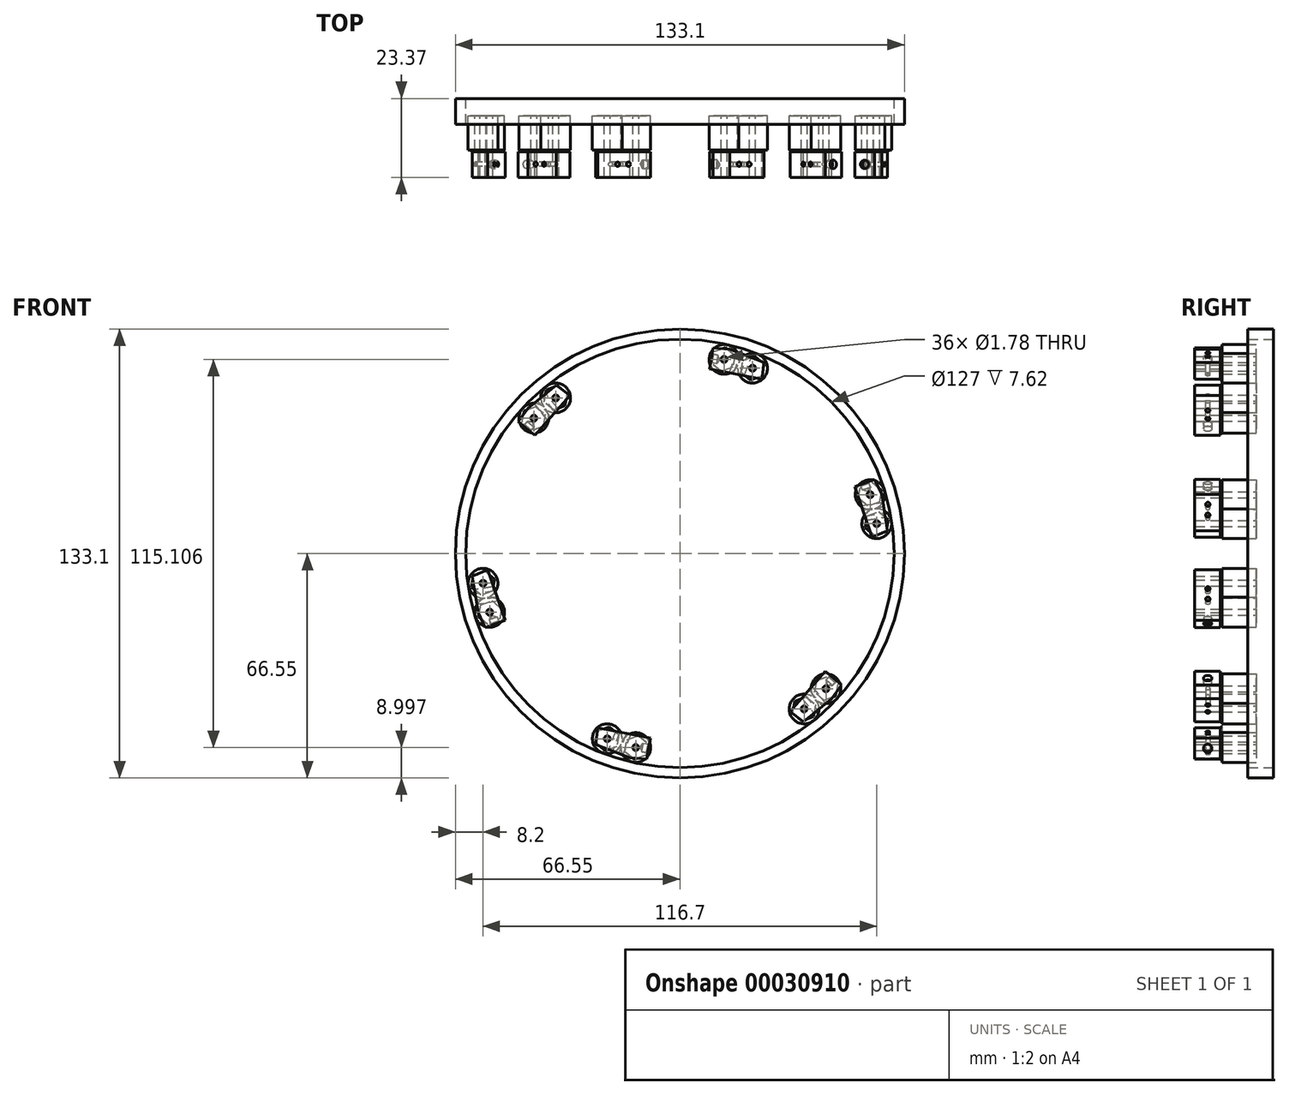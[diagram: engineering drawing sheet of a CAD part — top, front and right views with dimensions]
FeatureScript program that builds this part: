
annotation { "Feature Type Name" : "Feature", "Feature Type Description" : "" }
export const myFeature = defineFeature(function(context is Context, id is Id, definition is map)
    precondition{}
    {
        {
            var Q0;
            Q0=qCreatedBy(makeId("Front.planeOp"),FACE);
            var sketch = newSketch(context, id + "F0", { "sketchPlane" : qUnion([Q0])});
            skCircle(sketch, "E0", {"center": v(0, 0) * mm, "radius": 66.55 * mm});
            skSolve(sketch);
        }
        {
            var Q0;
            Q0=makeQuery(id+"F0.imprint","IMPRINT",FACE,{"disambiguationData":[TD([[makeQuery(id+"F0.imprint","IMPRINT",EDGE,{"derivedFrom":sQuery(id+"F0.wireOp",EDGE,"E0")}),1.0]])]});
            extrude(context, id + "F1", {"entities" : qUnion([Q0]), "depth" : 7.62 * mm});
        }
        {
            var Q0;
            Q0=sQuery(id+"F0.wireOp",VERTEX,"E0.center");
            var Q1;
            Q1=makeQuery(id+"F1.opExtrude","SWEPT_BODY",BODY,{"disambiguationData":[OSD([sQuery(id+"F0.wireOp",EDGE,"E0")])]});
            hole(context, id + "F2", {"style" : HoleStyle.SIMPLE, "holeDiameter" : 127 * mm, "endStyle" : HoleEndStyle.THROUGH, "oppositeDirection" : true, "locations" : qUnion([Q0]), "scope" : qUnion([Q1])});
        }
        {
            var Q0;
            Q0=qCreatedBy(makeId("Front.planeOp"),FACE);
            var sketch = newSketch(context, id + "F3", { "sketchPlane" : qUnion([Q0])});
            skCircle(sketch, "E1", {"center": v(13.1, 57.55) * mm, "radius": 4.4 * mm});
            skPoint(sketch, "E1.first.point", {"position": v(14.07, 61.85) * mm});
            skPoint(sketch, "E1.second.point", {"position": v(11.49, 53.45) * mm});
            skPoint(sketch, "E1.third.point", {"position": v(11.97, 53.29) * mm});
            skCircle(sketch, "E2", {"center": v(21.53, 54.95) * mm, "radius": 4.4 * mm});
            skSolve(sketch);
        }
        {
            var Q0;
            Q0=makeQuery(id+"F3.imprint","IMPRINT",FACE,{"disambiguationData":[TD([[makeQuery(id+"F3.imprint","IMPRINT",EDGE,{"derivedFrom":sQuery(id+"F3.wireOp",EDGE,"E2")}),1.0]])]});
            var Q1;
            Q1=makeQuery(id+"F3.imprint","IMPRINT",FACE,{"disambiguationData":[TD([[makeQuery(id+"F3.imprint","IMPRINT",EDGE,{"derivedFrom":sQuery(id+"F3.wireOp",EDGE,"E1")}),1.0]])]});
            extrude(context, id + "F4", {"entities" : qUnion([Q0, Q1]), "depth" : 15.24 * mm, "hasSecondDirection" : true, "secondDirectionOppositeDirection" : false, "secondDirectionDepth" : 5.08 * mm});
        }
        {
            var Q0;
            Q0=makeQuery(id+"F4.opExtrude","CAP_FACE",FACE,{"disambiguationData":[OSD([sQuery(id+"F3.wireOp",EDGE,"E2")])],"isStart":false});
            var sketch = newSketch(context, id + "F5", { "sketchPlane" : qUnion([Q0])});
            skCircle(sketch, "E3.cCircle", {"center": v(21.53, 54.95) * mm, "radius": 3.13 * mm, "construction": true});
            skLineSegment(sketch, "E3.0", {"start": v(24.3, 52.62) * mm, "end": v(20.9, 51.39) * mm});
            skLineSegment(sketch, "E3.1", {"start": v(20.9, 51.39) * mm, "end": v(18.14, 53.71) * mm});
            skLineSegment(sketch, "E3.2", {"start": v(18.14, 53.71) * mm, "end": v(18.77, 57.27) * mm});
            skLineSegment(sketch, "E3.3", {"start": v(18.77, 57.27) * mm, "end": v(22.16, 58.5) * mm});
            skLineSegment(sketch, "E3.4", {"start": v(22.16, 58.5) * mm, "end": v(24.93, 56.18) * mm});
            skLineSegment(sketch, "E3.5", {"start": v(24.93, 56.18) * mm, "end": v(24.3, 52.62) * mm});
            skPoint(sketch, "E3.0.midPoint", {"position": v(22.6, 52) * mm});
            skLineSegment(sketch, "E4.1", {"start": v(12.3, 54) * mm, "end": v(9.52, 56.32) * mm});
            skLineSegment(sketch, "E4.2", {"start": v(9.52, 56.32) * mm, "end": v(10.16, 59.88) * mm});
            skLineSegment(sketch, "E4.3", {"start": v(10.16, 59.88) * mm, "end": v(13.55, 61.11) * mm});
            skLineSegment(sketch, "E4.4", {"start": v(13.55, 61.11) * mm, "end": v(16.32, 58.79) * mm});
            skLineSegment(sketch, "E4.5", {"start": v(16.32, 58.79) * mm, "end": v(15.69, 55.23) * mm});
            skLineSegment(sketch, "E4.0", {"start": v(15.69, 55.23) * mm, "end": v(12.3, 54) * mm});
            skCircle(sketch, "E4.cCircle", {"center": v(12.92, 57.55) * mm, "radius": 3.13 * mm, "construction": true});
            skSolve(sketch);
        }
        {
            var Q0;
            Q0=makeQuery(id+"F5.imprint","IMPRINT",FACE,{"disambiguationData":[TD([[makeQuery(id+"F5.imprint","IMPRINT",EDGE,{"derivedFrom":sQuery(id+"F5.wireOp",EDGE,"E3.0")}),-1.0]])]});
            var Q1;
            Q1=makeQuery(id+"F5.imprint","IMPRINT",FACE,{"disambiguationData":[TD([[makeQuery(id+"F5.imprint","IMPRINT",EDGE,{"derivedFrom":sQuery(id+"F5.wireOp",EDGE,"E4.1")}),-1.0]])]});
            extrude(context, id + "F6", {"entities" : qUnion([Q0, Q1]), "depth" : 0.5 * mm});
        }
        {
            var Q0;
            Q0=makeQuery(id+"F6.opExtrude","CAP_FACE",FACE,{"disambiguationData":[OSD([sQuery(id+"F5.wireOp",EDGE,"E3.0"),sQuery(id+"F5.wireOp",EDGE,"E3.1"),sQuery(id+"F5.wireOp",EDGE,"E3.2"),sQuery(id+"F5.wireOp",EDGE,"E3.3"),sQuery(id+"F5.wireOp",EDGE,"E3.4"),sQuery(id+"F5.wireOp",EDGE,"E3.5")])],"isStart":false});
            var sketch = newSketch(context, id + "F7", { "sketchPlane" : qUnion([Q0])});
            skLineSegment(sketch, "E5", {"start": v(24.3, 51.72) * mm, "end": v(24.93, 56.67) * mm});
            skLineSegment(sketch, "E6", {"start": v(24.93, 56.67) * mm, "end": v(14.76, 60.55) * mm});
            skLineSegment(sketch, "E7", {"start": v(14.76, 60.55) * mm, "end": v(9.87, 61) * mm});
            skLineSegment(sketch, "E8", {"start": v(9.87, 61) * mm, "end": v(8.76, 54.78) * mm});
            skLineSegment(sketch, "E9", {"start": v(8.76, 54.78) * mm, "end": v(24.3, 51.72) * mm});
            skSolve(sketch);
        }
        {
            var Q0;
            {var subQ8=sQuery(id+"F7.wireOp",EDGE,"E7");Q0=makeQuery(id+"F7.imprint","IMPRINT",FACE,{"disambiguationData":[TD([[makeQuery(id+"F7.imprint","IMPRINT",EDGE,{"derivedFrom":subQ8}),1.0]])]});}
            var Q1;
            {var subQ11=makeQuery(id+"F6.opExtrude","CAP_EDGE",EDGE,{"disambiguationData":[OSD([sQuery(id+"F5.wireOp",EDGE,"E3.2")])],"isStart":false});Q1=makeQuery(id+"F7.imprint","IMPRINT",FACE,{"disambiguationData":[TD([[makeQuery(id+"F7.imprint","IMPRINT",EDGE,{"derivedFrom":subQ11}),-1.0]])]});}
            var Q2;
            {var subQ1=sQuery(id+"F7.wireOp",EDGE,"E5");var subQ5=sQuery(id+"F7.wireOp",EDGE,"E9");var subQ7=makeQuery(id+"F7.imprint","INTERSECT",VERTEX,{"derivedFrom":[subQ1,subQ5]});Q2=makeQuery(id+"F7.imprint","IMPRINT",FACE,{"disambiguationData":[TD([[makeQuery(id+"F7.imprint","IMPRINT",EDGE,{"disambiguationData":[TD([[subQ7,-1.0]])],"derivedFrom":subQ1}),1.0]])]});}
            var Q3;
            {var subQ1=sQuery(id+"F7.wireOp",EDGE,"E6");var subQ3=sQuery(id+"F7.wireOp",EDGE,"E5");var subQ5=makeQuery(id+"F7.imprint","INTERSECT",VERTEX,{"derivedFrom":[subQ3,subQ1]});Q3=makeQuery(id+"F7.imprint","IMPRINT",FACE,{"disambiguationData":[TD([[makeQuery(id+"F7.imprint","IMPRINT",EDGE,{"disambiguationData":[TD([[subQ5,1.0]])],"derivedFrom":subQ3}),1.0]])]});}
            extrude(context, id + "F8", {"entities" : qUnion([Q0, Q1, Q2, Q3]), "depth" : 7.62 * mm});
        }
        {
            var Q0;
            Q0=sQuery(id+"F3.wireOp",VERTEX,"E2.center");
            var Q1;
            Q1=makeQuery(id+"F4.opExtrude","SWEPT_BODY",BODY,{"disambiguationData":[OSD([sQuery(id+"F3.wireOp",EDGE,"E2")])]});
            var Q2;
            Q2=makeQuery(id+"F6.opExtrude","SWEPT_BODY",BODY,{"disambiguationData":[OSD([sQuery(id+"F5.wireOp",EDGE,"E3.0"),sQuery(id+"F5.wireOp",EDGE,"E3.1"),sQuery(id+"F5.wireOp",EDGE,"E3.2"),sQuery(id+"F5.wireOp",EDGE,"E3.3"),sQuery(id+"F5.wireOp",EDGE,"E3.4"),sQuery(id+"F5.wireOp",EDGE,"E3.5")])]});
            var Q3;
            Q3=makeQuery(id+"F8.opExtrude","SWEPT_BODY",BODY,{"disambiguationData":[OSD([sQuery(id+"F7.wireOp",EDGE,"E5"),sQuery(id+"F7.wireOp",EDGE,"E6"),sQuery(id+"F7.wireOp",EDGE,"E7"),sQuery(id+"F7.wireOp",EDGE,"E8"),sQuery(id+"F7.wireOp",EDGE,"E9")])]});
            hole(context, id + "F9", {"style" : HoleStyle.SIMPLE, "holeDiameter" : 1.78 * mm, "endStyle" : HoleEndStyle.THROUGH, "oppositeDirection" : true, "locations" : qUnion([Q0]), "scope" : qUnion([Q1, Q2, Q3])});
        }
        {
            var Q0;
            Q0=sQuery(id+"F3.wireOp",VERTEX,"E1.center");
            var Q1;
            Q1=makeQuery(id+"F4.opExtrude","SWEPT_BODY",BODY,{"disambiguationData":[OSD([sQuery(id+"F3.wireOp",EDGE,"E1")])]});
            var Q2;
            Q2=makeQuery(id+"F6.opExtrude","SWEPT_BODY",BODY,{"disambiguationData":[OSD([sQuery(id+"F5.wireOp",EDGE,"E4.1"),sQuery(id+"F5.wireOp",EDGE,"E4.2"),sQuery(id+"F5.wireOp",EDGE,"E4.3"),sQuery(id+"F5.wireOp",EDGE,"E4.4"),sQuery(id+"F5.wireOp",EDGE,"E4.5"),sQuery(id+"F5.wireOp",EDGE,"E4.0")])]});
            var Q3;
            Q3=makeQuery(id+"F8.opExtrude","SWEPT_BODY",BODY,{"disambiguationData":[OSD([sQuery(id+"F7.wireOp",EDGE,"E5"),sQuery(id+"F7.wireOp",EDGE,"E6"),sQuery(id+"F7.wireOp",EDGE,"E7"),sQuery(id+"F7.wireOp",EDGE,"E8"),sQuery(id+"F7.wireOp",EDGE,"E9")])]});
            hole(context, id + "F10", {"style" : HoleStyle.SIMPLE, "holeDiameter" : 1.78 * mm, "endStyle" : HoleEndStyle.THROUGH, "oppositeDirection" : true, "locations" : qUnion([Q0]), "scope" : qUnion([Q1, Q2, Q3])});
        }
        {
            var Q0;
            Q0=makeQuery(id+"F8.opExtrude","SWEPT_FACE",FACE,{"disambiguationData":[OSD([sQuery(id+"F7.wireOp",EDGE,"E6")])]});
            var sketch = newSketch(context, id + "F11", { "sketchPlane" : qUnion([Q0])});
            skCircle(sketch, "E10", {"center": v(-4.86, -19.5) * mm, "radius": 0.82 * mm});
            skCircle(sketch, "E11", {"center": v(-1.64, -19.51) * mm, "radius": 0.82 * mm});
            skSolve(sketch);
        }
        {
            var Q0;
            Q0=sQuery(id+"F11.wireOp",VERTEX,"E10.center");
            var Q1;
            Q1=sQuery(id+"F11.wireOp",VERTEX,"E11.center");
            var Q2;
            Q2=makeQuery(id+"F8.opExtrude","SWEPT_BODY",BODY,{"disambiguationData":[OSD([sQuery(id+"F7.wireOp",EDGE,"E5"),sQuery(id+"F7.wireOp",EDGE,"E6"),sQuery(id+"F7.wireOp",EDGE,"E7"),sQuery(id+"F7.wireOp",EDGE,"E8"),sQuery(id+"F7.wireOp",EDGE,"E9")])]});
            hole(context, id + "F12", {"style" : HoleStyle.SIMPLE, "holeDiameter" : 1.27 * mm, "endStyle" : HoleEndStyle.THROUGH, "locations" : qUnion([Q0, Q1]), "scope" : qUnion([Q2])});
        }
        {
            var Q0;
            Q0=makeQuery(id+"F8.opExtrude","SWEPT_FACE",FACE,{"disambiguationData":[OSD([sQuery(id+"F7.wireOp",EDGE,"E8")])]});
            var sketch = newSketch(context, id + "F13", { "sketchPlane" : qUnion([Q0])});
            skCircle(sketch, "E12", {"center": v(19.55, 58.57) * mm, "radius": 1.19 * mm});
            skSolve(sketch);
        }
        {
            var Q0;
            Q0=sQuery(id+"F13.wireOp",VERTEX,"E12.center");
            var Q1;
            Q1=makeQuery(id+"F8.opExtrude","SWEPT_BODY",BODY,{"disambiguationData":[OSD([sQuery(id+"F7.wireOp",EDGE,"E5"),sQuery(id+"F7.wireOp",EDGE,"E6"),sQuery(id+"F7.wireOp",EDGE,"E7"),sQuery(id+"F7.wireOp",EDGE,"E8"),sQuery(id+"F7.wireOp",EDGE,"E9")])]});
            hole(context, id + "F14", {"style" : HoleStyle.SIMPLE, "holeDiameter" : 2.54 * mm, "endStyle" : HoleEndStyle.BLIND, "holeDepth" : 1.78 * mm, "locations" : qUnion([Q0]), "scope" : qUnion([Q1])});
        }
        {
            var Q0;
            Q0=makeQuery(id+"F4.opExtrude","SWEPT_BODY",BODY,{"disambiguationData":[OSD([sQuery(id+"F3.wireOp",EDGE,"E1")])]});
            var Q1;
            Q1=makeQuery(id+"F4.opExtrude","SWEPT_BODY",BODY,{"disambiguationData":[OSD([sQuery(id+"F3.wireOp",EDGE,"E2")])]});
            var Q2;
            Q2=makeQuery(id+"F6.opExtrude","SWEPT_BODY",BODY,{"disambiguationData":[OSD([sQuery(id+"F5.wireOp",EDGE,"E4.1"),sQuery(id+"F5.wireOp",EDGE,"E4.2"),sQuery(id+"F5.wireOp",EDGE,"E4.3"),sQuery(id+"F5.wireOp",EDGE,"E4.4"),sQuery(id+"F5.wireOp",EDGE,"E4.5"),sQuery(id+"F5.wireOp",EDGE,"E4.0")])]});
            var Q3;
            Q3=makeQuery(id+"F6.opExtrude","SWEPT_BODY",BODY,{"disambiguationData":[OSD([sQuery(id+"F5.wireOp",EDGE,"E3.0"),sQuery(id+"F5.wireOp",EDGE,"E3.1"),sQuery(id+"F5.wireOp",EDGE,"E3.2"),sQuery(id+"F5.wireOp",EDGE,"E3.3"),sQuery(id+"F5.wireOp",EDGE,"E3.4"),sQuery(id+"F5.wireOp",EDGE,"E3.5")])]});
            var Q4;
            Q4=makeQuery(id+"F8.opExtrude","SWEPT_BODY",BODY,{"disambiguationData":[OSD([sQuery(id+"F7.wireOp",EDGE,"E5"),sQuery(id+"F7.wireOp",EDGE,"E6"),sQuery(id+"F7.wireOp",EDGE,"E7"),sQuery(id+"F7.wireOp",EDGE,"E8"),sQuery(id+"F7.wireOp",EDGE,"E9")])]});
            var Q5;
            Q5=sQuery(id+"F0.wireOp",EDGE,"E0");
            circularPattern(context, id + "F15", {"entities" : qUnion([Q0, Q1, Q2, Q3, Q4]), "axis" : qUnion([Q5]), "angle" : 60 * degree, "instanceCount" : 6});
        }
    });
